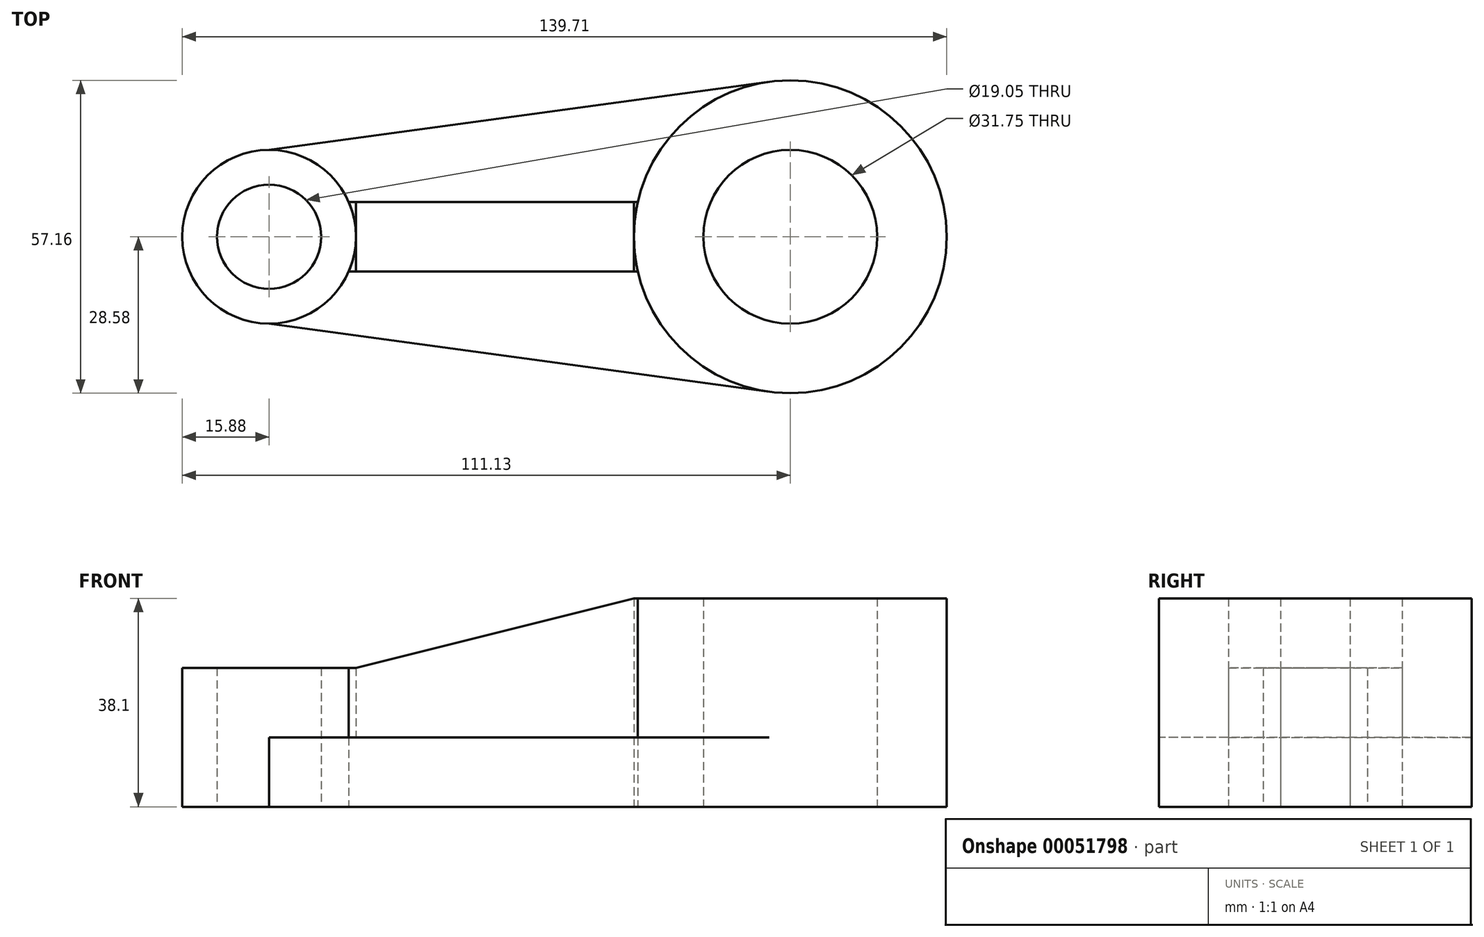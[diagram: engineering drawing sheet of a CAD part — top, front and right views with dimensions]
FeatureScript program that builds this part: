
annotation { "Feature Type Name" : "Feature", "Feature Type Description" : "" }
export const myFeature = defineFeature(function(context is Context, id is Id, definition is map)
    precondition{}
    {
        {
            var Q0;
            Q0=qCreatedBy(makeId("Top.planeOp"),FACE);
            var sketch = newSketch(context, id + "F0", { "sketchPlane" : qUnion([Q0])});
            skCircle(sketch, "E0", {"center": v(0, 0) * mm, "radius": 28.58 * mm});
            skLineSegment(sketch, "E1", {"start": v(0, 0) * mm, "end": v(-95.25, 0) * mm, "construction": true});
            skCircle(sketch, "E2", {"center": v(0, 0) * mm, "radius": 15.88 * mm});
            skCircle(sketch, "E3", {"center": v(-95.25, 0) * mm, "radius": 15.88 * mm});
            skCircle(sketch, "E4", {"center": v(-95.25, 0) * mm, "radius": 9.53 * mm});
            skLineSegment(sketch, "E5", {"start": v(-27.86, 6.35) * mm, "end": v(-80.7, 6.35) * mm});
            skLineSegment(sketch, "E6", {"start": v(-27.86, -6.35) * mm, "end": v(-80.7, -6.35) * mm});
            skLineSegment(sketch, "E7", {"start": v(-95.25, 0) * mm, "end": v(-95.25, 22.4) * mm, "construction": true});
            skLineSegment(sketch, "E8", {"start": v(-95.25, 15.87) * mm, "end": v(0, 28.84) * mm});
            skLineSegment(sketch, "E9", {"start": v(0, 0) * mm, "end": v(0, 28.58) * mm, "construction": true});
            skLineSegment(sketch, "E10", {"start": v(-95.25, -15.87) * mm, "end": v(0, -28.84) * mm});
            skLineSegment(sketch, "E11", {"start": v(0, 0) * mm, "end": v(0, -28.84) * mm, "construction": true});
            skSolve(sketch);
        }
        {
            var Q0;
            Q0=makeQuery(id+"F0.imprint","IMPRINT",FACE,{"disambiguationData":[TD([[makeQuery(id+"F0.imprint","IMPRINT",EDGE,{"derivedFrom":sQuery(id+"F0.wireOp",EDGE,"E4")}),-1.0]])]});
            var Q1;
            {var subQ0=sQuery(id+"F0.wireOp",EDGE,"E5");Q1=makeQuery(id+"F0.imprint","IMPRINT",FACE,{"disambiguationData":[TD([[makeQuery(id+"F0.imprint","IMPRINT",EDGE,{"derivedFrom":subQ0}),1.0]])]});}
            var Q2;
            {var subQ0=sQuery(id+"F0.wireOp",EDGE,"E5");Q2=makeQuery(id+"F0.imprint","IMPRINT",FACE,{"disambiguationData":[TD([[makeQuery(id+"F0.imprint","IMPRINT",EDGE,{"derivedFrom":subQ0}),-1.0]])]});}
            var Q3;
            {var subQ0=sQuery(id+"F0.wireOp",EDGE,"E6");Q3=makeQuery(id+"F0.imprint","IMPRINT",FACE,{"disambiguationData":[TD([[makeQuery(id+"F0.imprint","IMPRINT",EDGE,{"derivedFrom":subQ0}),1.0]])]});}
            var Q4;
            Q4=makeQuery(id+"F0.imprint","IMPRINT",FACE,{"disambiguationData":[TD([[makeQuery(id+"F0.imprint","IMPRINT",EDGE,{"derivedFrom":sQuery(id+"F0.wireOp",EDGE,"E2")}),-1.0]])]});
            extrude(context, id + "F1", {"entities" : qUnion([Q0, Q1, Q2, Q3, Q4]), "depth" : 12.7 * mm});
        }
        {
            var Q0;
            Q0=makeQuery(id+"F0.imprint","IMPRINT",FACE,{"disambiguationData":[TD([[makeQuery(id+"F0.imprint","IMPRINT",EDGE,{"derivedFrom":sQuery(id+"F0.wireOp",EDGE,"E2")}),-1.0]])]});
            extrude(context, id + "F2", {"entities" : qUnion([Q0]), "operationType" : NewBodyOperationType.ADD, "depth" : 38.1 * mm});
        }
        {
            var Q0;
            Q0=makeQuery(id+"F0.imprint","IMPRINT",FACE,{"disambiguationData":[TD([[makeQuery(id+"F0.imprint","IMPRINT",EDGE,{"derivedFrom":sQuery(id+"F0.wireOp",EDGE,"E4")}),-1.0]])]});
            extrude(context, id + "F3", {"entities" : qUnion([Q0]), "operationType" : NewBodyOperationType.ADD, "depth" : 25.4 * mm});
        }
        {
            var Q0;
            Q0=qCreatedBy(makeId("Front.planeOp"),FACE);
            var sketch = newSketch(context, id + "F4", { "sketchPlane" : qUnion([Q0])});
            skLineSegment(sketch, "E12", {"start": v(-79.38, 12.7) * mm, "end": v(-28.58, 12.7) * mm});
            skLineSegment(sketch, "E13", {"start": v(-79.38, 25.4) * mm, "end": v(-28.58, 38.1) * mm});
            skLineSegment(sketch, "E14", {"start": v(0, 0) * mm, "end": v(-28.58, 0) * mm, "construction": true});
            skLineSegment(sketch, "E15", {"start": v(-28.58, 0) * mm, "end": v(-28.58, 38.1) * mm, "construction": true});
            skLineSegment(sketch, "E16", {"start": v(-79.38, 25.4) * mm, "end": v(-79.38, 0) * mm, "construction": true});
            skLineSegment(sketch, "E17", {"start": v(-79.38, 0) * mm, "end": v(-95.25, 0) * mm, "construction": true});
            skLineSegment(sketch, "E18", {"start": v(-79.38, 25.4) * mm, "end": v(-79.38, 12.7) * mm});
            skLineSegment(sketch, "E19", {"start": v(-28.58, 38.1) * mm, "end": v(-28.58, 12.7) * mm});
            skSolve(sketch);
        }
        {
            var Q0;
            {var subQ0=sQuery(id+"F0.wireOp",EDGE,"E5");Q0=makeQuery(id+"F0.imprint","IMPRINT",FACE,{"disambiguationData":[TD([[makeQuery(id+"F0.imprint","IMPRINT",EDGE,{"derivedFrom":subQ0}),1.0]])]});}
            var Q1;
            Q1=makeQuery(id+"F2.opExtrude","CAP_FACE",FACE,{"disambiguationData":[OSD([sQuery(id+"F0.wireOp",EDGE,"E0"),sQuery(id+"F0.wireOp",EDGE,"E2")])],"isStart":false});
            extrude(context, id + "F5", {"entities" : qUnion([Q0]), "endBound" : BoundingType.UP_TO_SURFACE, "endBoundEntityFace" : qUnion([Q1]), "depth" : 25.4 * mm});
        }
        {
            var Q0;
            Q0=qCreatedBy(makeId("Front.planeOp"),FACE);
            var sketch = newSketch(context, id + "F6", { "sketchPlane" : qUnion([Q0])});
            skLineSegment(sketch, "E20", {"start": v(-79.38, 25.4) * mm, "end": v(-28.57, 38.1) * mm});
            skLineSegment(sketch, "E21", {"start": v(-79.38, 25.4) * mm, "end": v(-80.7, 25.4) * mm});
            skLineSegment(sketch, "E22", {"start": v(-80.7, 25.4) * mm, "end": v(-80.7, 38.1) * mm});
            skLineSegment(sketch, "E23", {"start": v(-80.7, 38.1) * mm, "end": v(-28.58, 38.1) * mm});
            skSolve(sketch);
        }
        {
            var Q0;
            Q0=makeQuery(id+"F6.imprint","IMPRINT",FACE,{"disambiguationData":[TD([[makeQuery(id+"F6.imprint","IMPRINT",EDGE,{"derivedFrom":sQuery(id+"F6.wireOp",EDGE,"E20")}),1.0]])]});
            var Q1;
            Q1=makeQuery(id+"F5.opExtrude","SWEPT_FACE",FACE,{"disambiguationData":[OSD([sQuery(id+"F0.wireOp",EDGE,"E5")])]});
            var Q2;
            Q2=makeQuery(id+"F5.opExtrude","SWEPT_FACE",FACE,{"disambiguationData":[OSD([sQuery(id+"F0.wireOp",EDGE,"E6")])]});
            extrude(context, id + "F7", {"entities" : qUnion([Q0]), "operationType" : NewBodyOperationType.REMOVE, "endBound" : BoundingType.UP_TO_SURFACE, "oppositeDirection" : true, "endBoundEntityFace" : qUnion([Q1]), "depth" : 25.4 * mm, "hasSecondDirection" : true, "secondDirectionBound" : SecondDirectionBoundingType.UP_TO_SURFACE, "secondDirectionOppositeDirection" : false, "secondDirectionBoundEntityFace" : qUnion([Q2]), "secondDirectionDepth" : 25.4 * mm});
        }
    });
